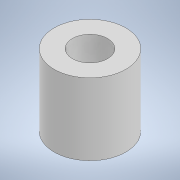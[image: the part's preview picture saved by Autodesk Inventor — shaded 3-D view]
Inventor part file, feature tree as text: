
AUTODESK INVENTOR PART (.ipt)
format: ipt  version: 2021 (Build 250183000, 183)  size: 230,912 bytes
history: native  units: mm
features: revolve x1, sketch x1
ambient origin geometry x8: Origin, YZ Plane, XZ Plane, XY Plane, X Axis, Y Axis, Z Axis, Center Point
bodies: Volumenkörper1 (feature_tree)
feature tree (2):
  revolve  "Umdrehung1"
  sketch  "Skizze1"  dims[d0=90.0deg d1=5.0mm d2=2.45mm d3=5.0mm d5=90.0deg]
